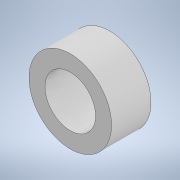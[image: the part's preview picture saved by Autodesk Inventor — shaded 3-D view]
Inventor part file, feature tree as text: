
AUTODESK INVENTOR PART (.ipt)
format: ipt  version: 2020 (Build 240168000, 168)  size: 98,304 bytes
history: native  units: mm
features: extrude x1, sketch x1
ambient origin geometry x8: Origin, YZ Plane, XZ Plane, XY Plane, X Axis, Y Axis, Z Axis, Center Point
bodies: Solid1 (feature_tree)
feature tree (2):
  extrude  "Extrusion1"  Depth=4.75mm
  sketch  "Sketch1"  dims[d0=9.95mm d1=6.1mm d2=4.75mm d3=0.0mm]
